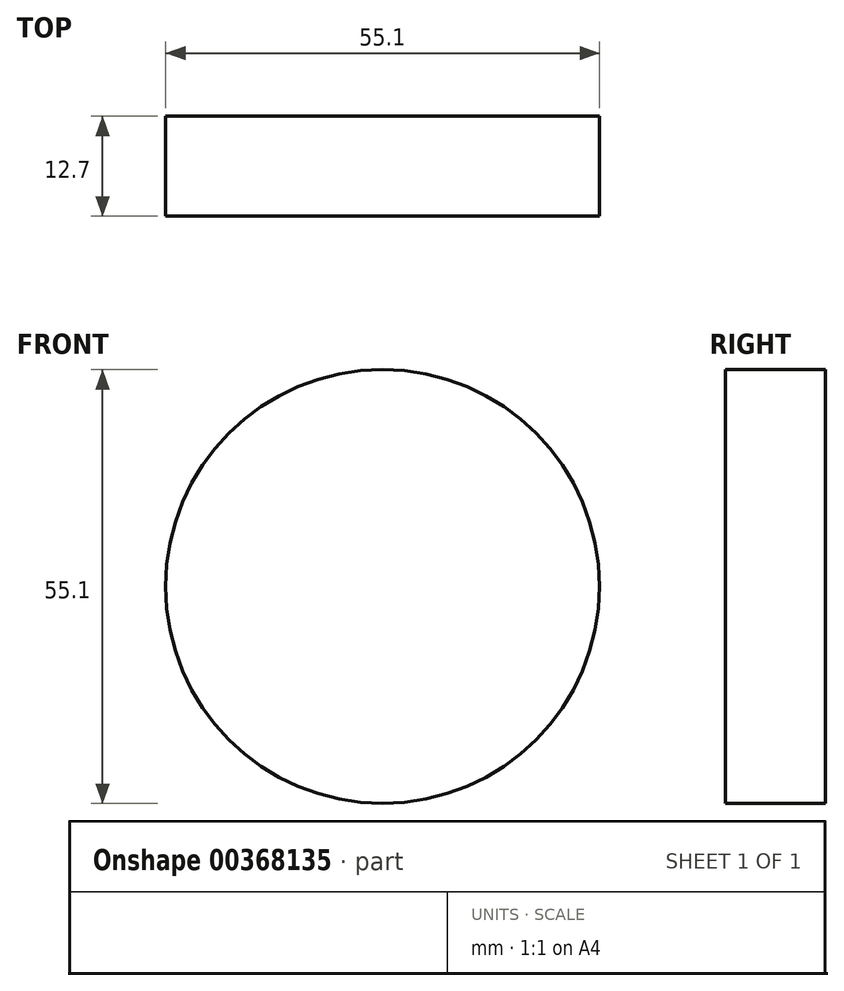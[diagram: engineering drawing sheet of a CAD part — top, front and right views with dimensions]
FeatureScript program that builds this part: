
annotation { "Feature Type Name" : "Feature", "Feature Type Description" : "" }
export const myFeature = defineFeature(function(context is Context, id is Id, definition is map)
    precondition{}
    {
        {
            var Q0;
            Q0=qCreatedBy(makeId("Front.planeOp"),FACE);
            var sketch = newSketch(context, id + "F0", { "sketchPlane" : qUnion([Q0])});
            skCircle(sketch, "E0", {"center": v(0, 0) * mm, "radius": 27.55 * mm});
            skCircle(sketch, "E1", {"center": v(0, 0) * mm, "radius": 57.53 * mm});
            skSolve(sketch);
        }
        {
            var Q0;
            Q0=makeQuery(id+"F0.imprint","IMPRINT",FACE,{"disambiguationData":[TD([[makeQuery(id+"F0.imprint","IMPRINT",EDGE,{"derivedFrom":sQuery(id+"F0.wireOp",EDGE,"E0")}),1.0]])]});
            extrude(context, id + "F1", {"entities" : qUnion([Q0]), "oppositeDirection" : true, "depth" : 12.7 * mm});
        }
    });
